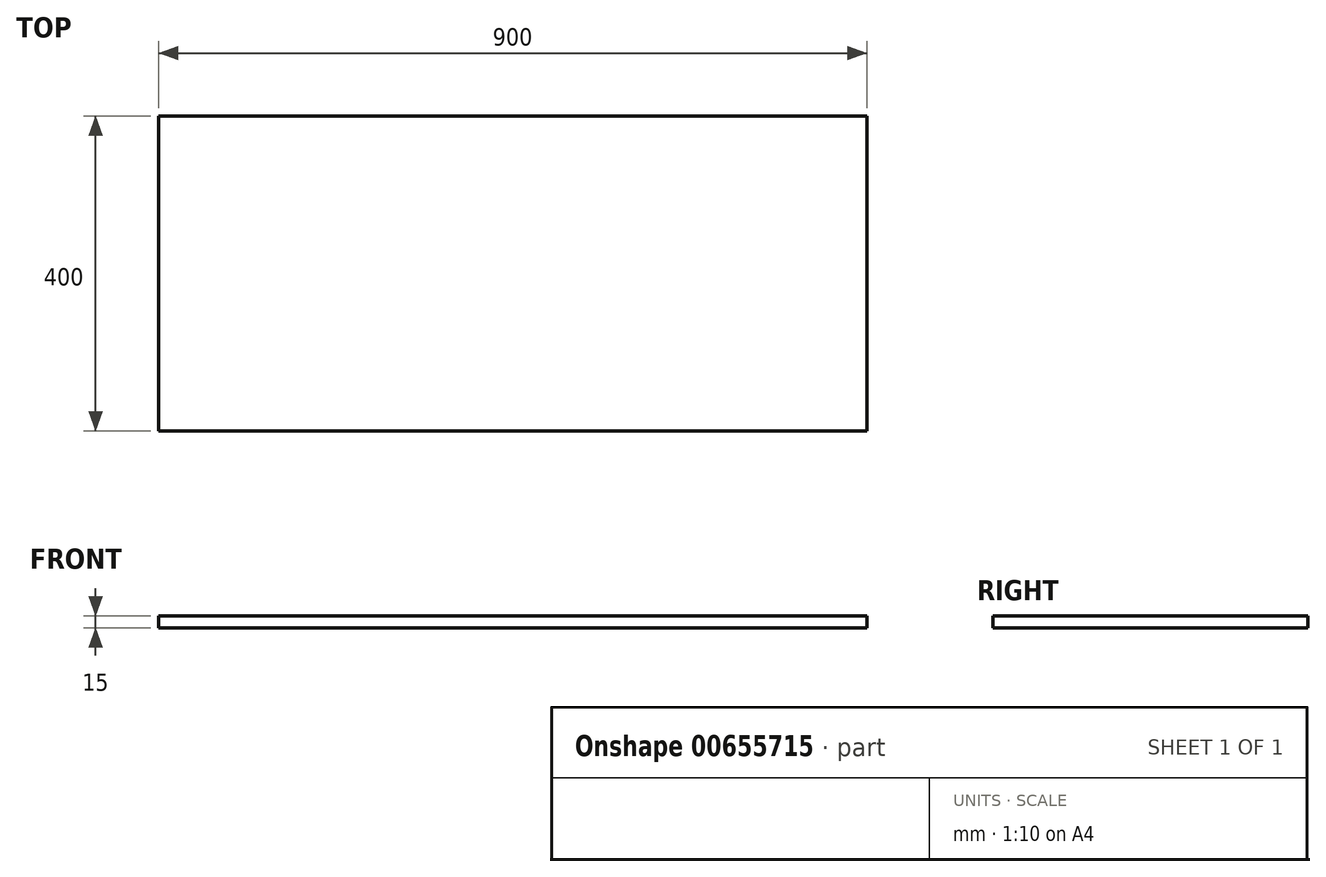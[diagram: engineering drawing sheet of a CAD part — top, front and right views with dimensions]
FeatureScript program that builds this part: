
annotation { "Feature Type Name" : "Feature", "Feature Type Description" : "" }
export const myFeature = defineFeature(function(context is Context, id is Id, definition is map)
    precondition{}
    {
        {
            var Q0;
            Q0=qCreatedBy(makeId("Top.planeOp"),FACE);
            var sketch = newSketch(context, id + "F0", { "sketchPlane" : qUnion([Q0])});
            skLineSegment(sketch, "E0.bottom", {"start": v(-900, 400) * mm, "end": v(0, 400) * mm});
            skLineSegment(sketch, "E0.top", {"start": v(-900, 0) * mm, "end": v(0, 0) * mm});
            skLineSegment(sketch, "E0.left", {"start": v(-900, 400) * mm, "end": v(-900, 0) * mm});
            skLineSegment(sketch, "E0.right", {"start": v(0, 400) * mm, "end": v(0, 0) * mm});
            skSolve(sketch);
        }
        {
            var Q0;
            Q0=makeQuery(id+"F0.imprint","IMPRINT",FACE,{"disambiguationData":[TD([[makeQuery(id+"F0.imprint","IMPRINT",EDGE,{"derivedFrom":sQuery(id+"F0.wireOp",EDGE,"E0.bottom")}),-1.0]])]});
            extrude(context, id + "F1", {"entities" : qUnion([Q0]), "depth" : 15 * mm, "offsetDistance" : 25 * mm});
        }
    });
